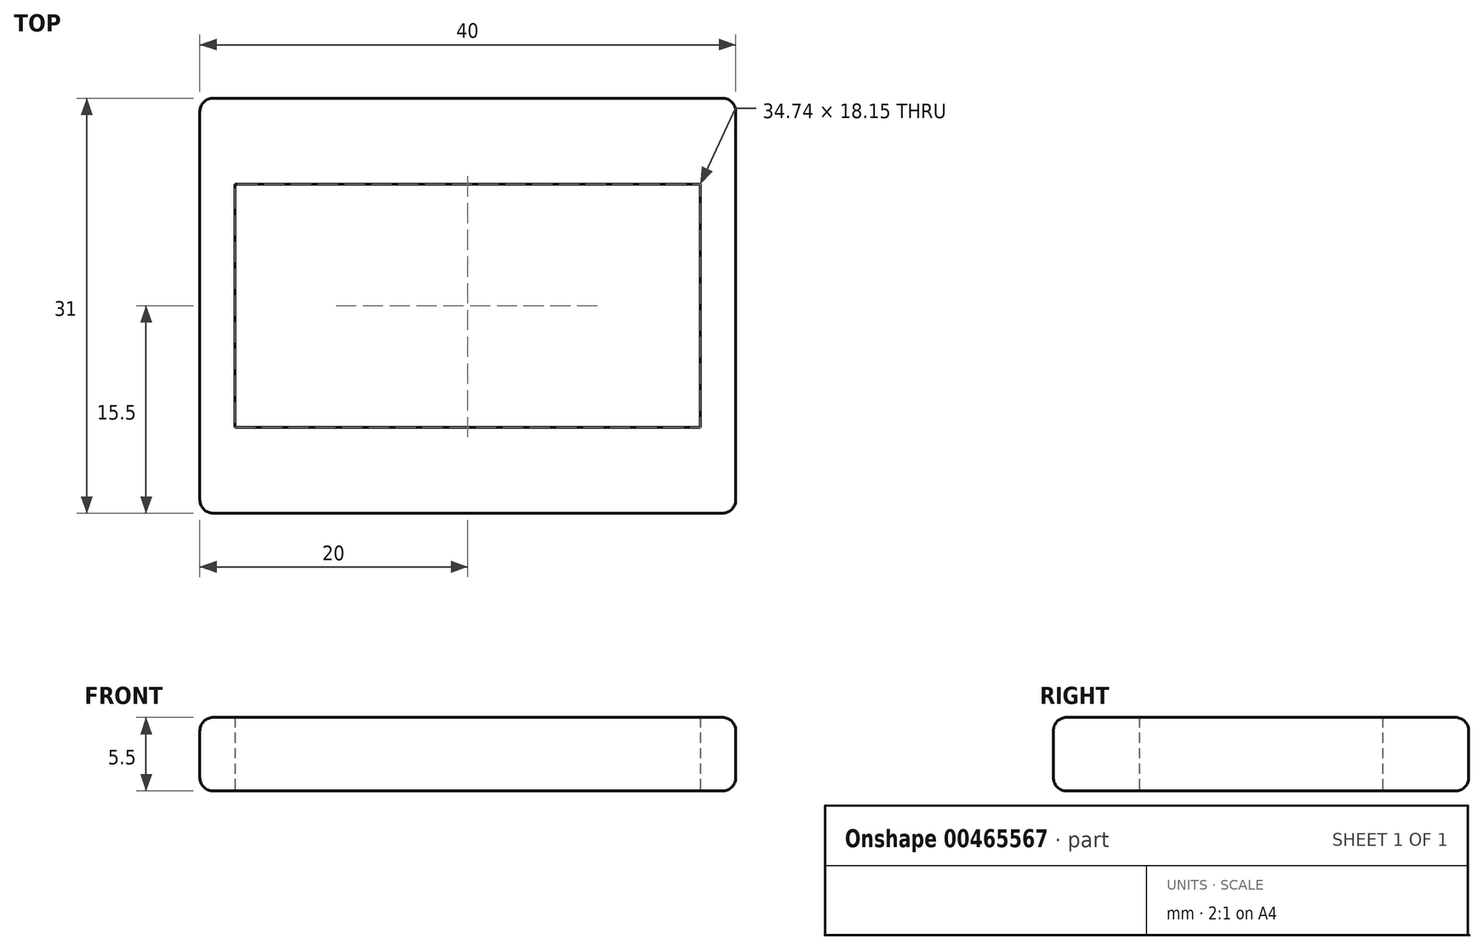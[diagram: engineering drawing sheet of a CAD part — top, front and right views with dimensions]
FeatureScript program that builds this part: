
annotation { "Feature Type Name" : "Feature", "Feature Type Description" : "" }
export const myFeature = defineFeature(function(context is Context, id is Id, definition is map)
    precondition{}
    {
        {
            var Q0;
            Q0=qCreatedBy(makeId("Top.planeOp"),FACE);
            var sketch = newSketch(context, id + "F0", { "sketchPlane" : qUnion([Q0])});
            skLineSegment(sketch, "E0.bottom", {"start": v(20, 15.5) * mm, "end": v(-20, 15.5) * mm});
            skLineSegment(sketch, "E0.top", {"start": v(20, -15.5) * mm, "end": v(-20, -15.5) * mm});
            skLineSegment(sketch, "E0.left", {"start": v(20, 15.5) * mm, "end": v(20, -15.5) * mm});
            skLineSegment(sketch, "E0.right", {"start": v(-20, 15.5) * mm, "end": v(-20, -15.5) * mm});
            skPoint(sketch, "E0.middle", {"position": v(0, 0) * mm});
            skSolve(sketch);
        }
        {
            var Q0;
            Q0=makeQuery(id+"F0.imprint","IMPRINT",FACE,{"disambiguationData":[TD([[makeQuery(id+"F0.imprint","IMPRINT",EDGE,{"derivedFrom":sQuery(id+"F0.wireOp",EDGE,"E0.bottom")}),1.0]])]});
            extrude(context, id + "F1", {"entities" : qUnion([Q0]), "depth" : 5.5 * mm});
        }
        {
            var Q0;
            Q0=makeQuery(id+"F1.opExtrude","CAP_FACE",FACE,{"disambiguationData":[OSD([sQuery(id+"F0.wireOp",EDGE,"E0.bottom"),sQuery(id+"F0.wireOp",EDGE,"E0.top"),sQuery(id+"F0.wireOp",EDGE,"E0.left"),sQuery(id+"F0.wireOp",EDGE,"E0.right")])],"isStart":false});
            var Q1;
            Q1=makeQuery(id+"F1.opExtrude","CAP_FACE",FACE,{"disambiguationData":[OSD([sQuery(id+"F0.wireOp",EDGE,"E0.bottom"),sQuery(id+"F0.wireOp",EDGE,"E0.top"),sQuery(id+"F0.wireOp",EDGE,"E0.left"),sQuery(id+"F0.wireOp",EDGE,"E0.right")])],"isStart":true});
            var Q2;
            Q2=makeQuery(id+"F1.opExtrude","SWEPT_FACE",FACE,{"disambiguationData":[OSD([sQuery(id+"F0.wireOp",EDGE,"E0.top")])]});
            var Q3;
            Q3=makeQuery(id+"F1.opExtrude","SWEPT_FACE",FACE,{"disambiguationData":[OSD([sQuery(id+"F0.wireOp",EDGE,"E0.right")])]});
            var Q4;
            Q4=makeQuery(id+"F1.opExtrude","SWEPT_FACE",FACE,{"disambiguationData":[OSD([sQuery(id+"F0.wireOp",EDGE,"E0.bottom")])]});
            fillet(context, id + "F2", {"entities" : qUnion([Q0, Q1, Q2, Q3, Q4]), "radius" : 1 * mm, "tangentPropagation" : true, "allowEdgeOverflow" : false});
        }
        {
            var Q0;
            Q0=makeQuery(id+"F1.opExtrude","CAP_FACE",FACE,{"disambiguationData":[OSD([sQuery(id+"F0.wireOp",EDGE,"E0.bottom"),sQuery(id+"F0.wireOp",EDGE,"E0.top"),sQuery(id+"F0.wireOp",EDGE,"E0.left"),sQuery(id+"F0.wireOp",EDGE,"E0.right")])],"isStart":true});
            var sketch = newSketch(context, id + "F3", { "sketchPlane" : qUnion([Q0])});
            skLineSegment(sketch, "E1.bottom", {"start": v(17.37, 9.07) * mm, "end": v(-17.37, 9.07) * mm});
            skLineSegment(sketch, "E1.top", {"start": v(17.37, -9.07) * mm, "end": v(-17.37, -9.07) * mm});
            skLineSegment(sketch, "E1.left", {"start": v(17.37, 9.07) * mm, "end": v(17.37, -9.07) * mm});
            skLineSegment(sketch, "E1.right", {"start": v(-17.37, 9.07) * mm, "end": v(-17.37, -9.07) * mm});
            skPoint(sketch, "E1.middle", {"position": v(0, 0) * mm});
            skSolve(sketch);
        }
        {
            var Q0;
            Q0=makeQuery(id+"F3.imprint","IMPRINT",FACE,{"disambiguationData":[TD([[makeQuery(id+"F3.imprint","IMPRINT",EDGE,{"derivedFrom":sQuery(id+"F3.wireOp",EDGE,"E1.bottom")}),1.0]])]});
            extrude(context, id + "F4", {"entities" : qUnion([Q0]), "operationType" : NewBodyOperationType.REMOVE, "oppositeDirection" : true, "depth" : 25 * mm, "offsetDistance" : 25 * mm});
        }
    });
